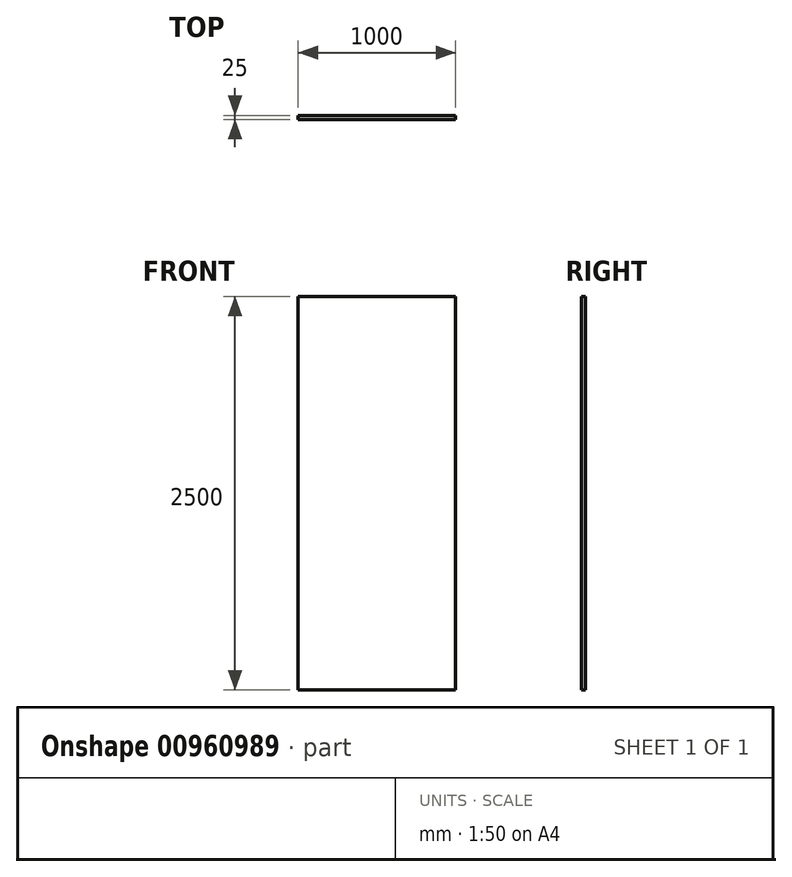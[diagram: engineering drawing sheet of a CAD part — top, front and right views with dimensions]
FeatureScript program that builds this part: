
annotation { "Feature Type Name" : "Feature", "Feature Type Description" : "" }
export const myFeature = defineFeature(function(context is Context, id is Id, definition is map)
    precondition{}
    {
        {
            var Q0;
            Q0=qCreatedBy(makeId("Front.planeOp"),FACE);
            var sketch = newSketch(context, id + "F0", { "sketchPlane" : qUnion([Q0])});
            skLineSegment(sketch, "E0.bottom", {"start": v(-2, 0) * mm, "end": v(998, 0) * mm});
            skLineSegment(sketch, "E0.top", {"start": v(-2, 2500) * mm, "end": v(998, 2500) * mm});
            skLineSegment(sketch, "E0.left", {"start": v(-2, 0) * mm, "end": v(-2, 2500) * mm});
            skLineSegment(sketch, "E0.right", {"start": v(998, 0) * mm, "end": v(998, 2500) * mm});
            skSolve(sketch);
        }
        {
            var Q0;
            Q0 = qSketchRegion(id + "F0", true);
            extrude(context, id + "F1", {"entities" : qUnion([Q0]), "depth" : 25 * mm, "offsetDistance" : 25 * mm});
        }
    });
